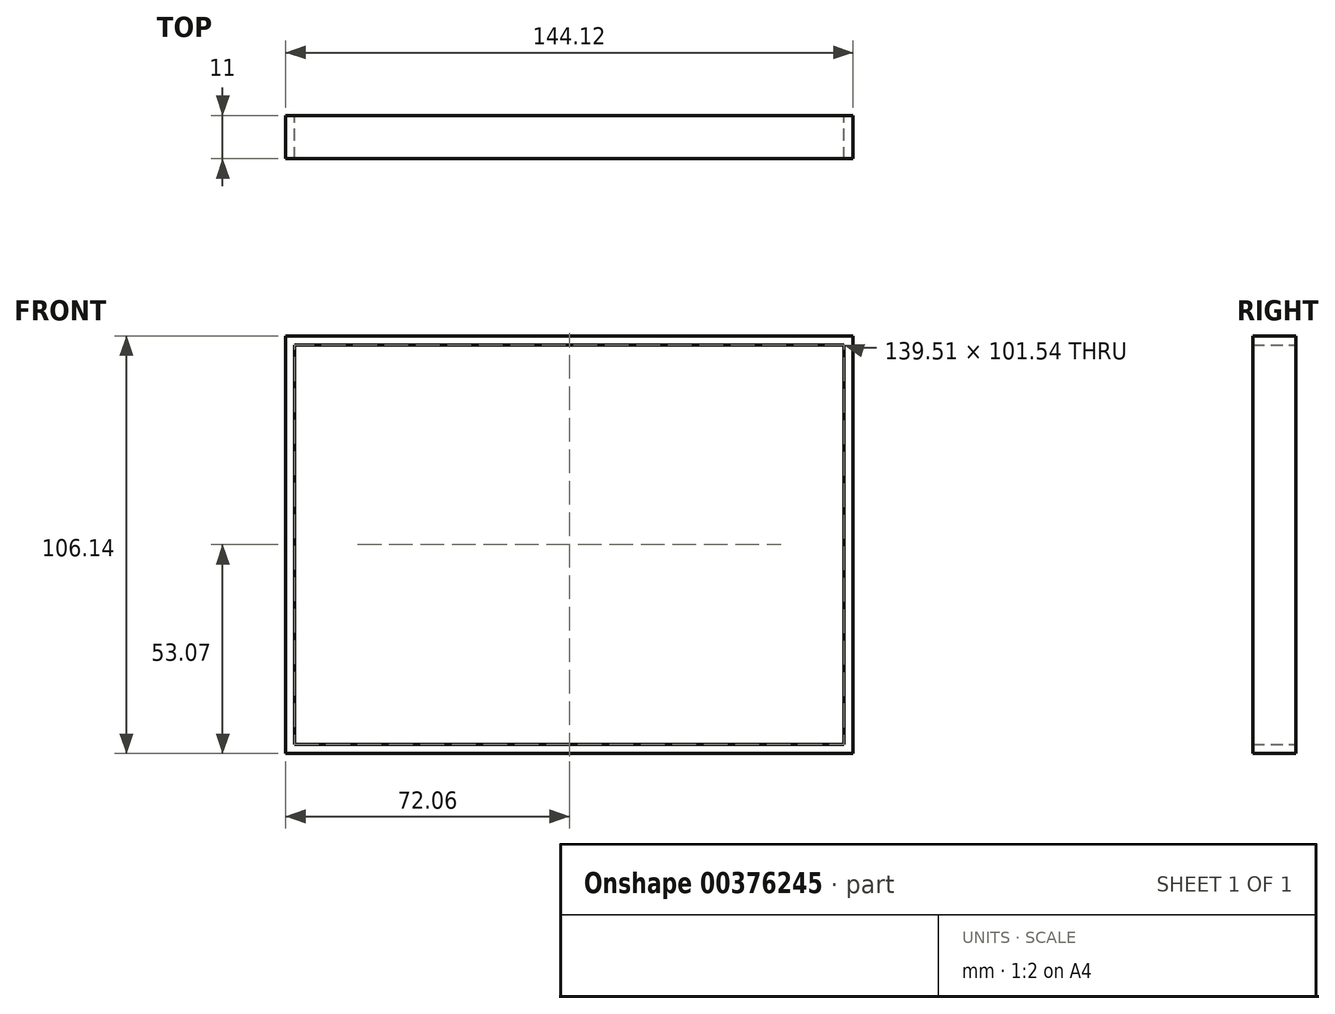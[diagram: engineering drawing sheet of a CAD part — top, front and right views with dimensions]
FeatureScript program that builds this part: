
annotation { "Feature Type Name" : "Feature", "Feature Type Description" : "" }
export const myFeature = defineFeature(function(context is Context, id is Id, definition is map)
    precondition{}
    {
        {
            var Q0;
            Q0=qCreatedBy(makeId("Front.planeOp"),FACE);
            var sketch = newSketch(context, id + "F0", { "sketchPlane" : qUnion([Q0])});
            skLineSegment(sketch, "E0.bottom", {"start": v(-69.76, 50.77) * mm, "end": v(69.76, 50.77) * mm});
            skLineSegment(sketch, "E0.top", {"start": v(-69.76, -50.77) * mm, "end": v(69.76, -50.77) * mm});
            skLineSegment(sketch, "E0.left", {"start": v(-69.76, 50.77) * mm, "end": v(-69.76, -50.77) * mm});
            skLineSegment(sketch, "E0.right", {"start": v(69.76, 50.77) * mm, "end": v(69.76, -50.77) * mm});
            skLineSegment(sketch, "E1.0", {"start": v(-72.06, 53.07) * mm, "end": v(72.06, 53.07) * mm});
            skLineSegment(sketch, "E1.1", {"start": v(-72.06, 53.07) * mm, "end": v(-72.06, -53.07) * mm});
            skLineSegment(sketch, "E1.2", {"start": v(-72.06, -53.07) * mm, "end": v(72.06, -53.07) * mm});
            skLineSegment(sketch, "E1.3", {"start": v(72.06, 53.07) * mm, "end": v(72.06, -53.07) * mm});
            skSolve(sketch);
        }
        {
            var Q0;
            Q0=makeQuery(id+"F0.imprint","IMPRINT",FACE,{"disambiguationData":[TD([[makeQuery(id+"F0.imprint","IMPRINT",EDGE,{"derivedFrom":sQuery(id+"F0.wireOp",EDGE,"E0.bottom")}),1.0]])]});
            extrude(context, id + "F1", {"entities" : qUnion([Q0]), "depth" : 11 * mm, "offsetDistance" : 25 * mm});
        }
    });
